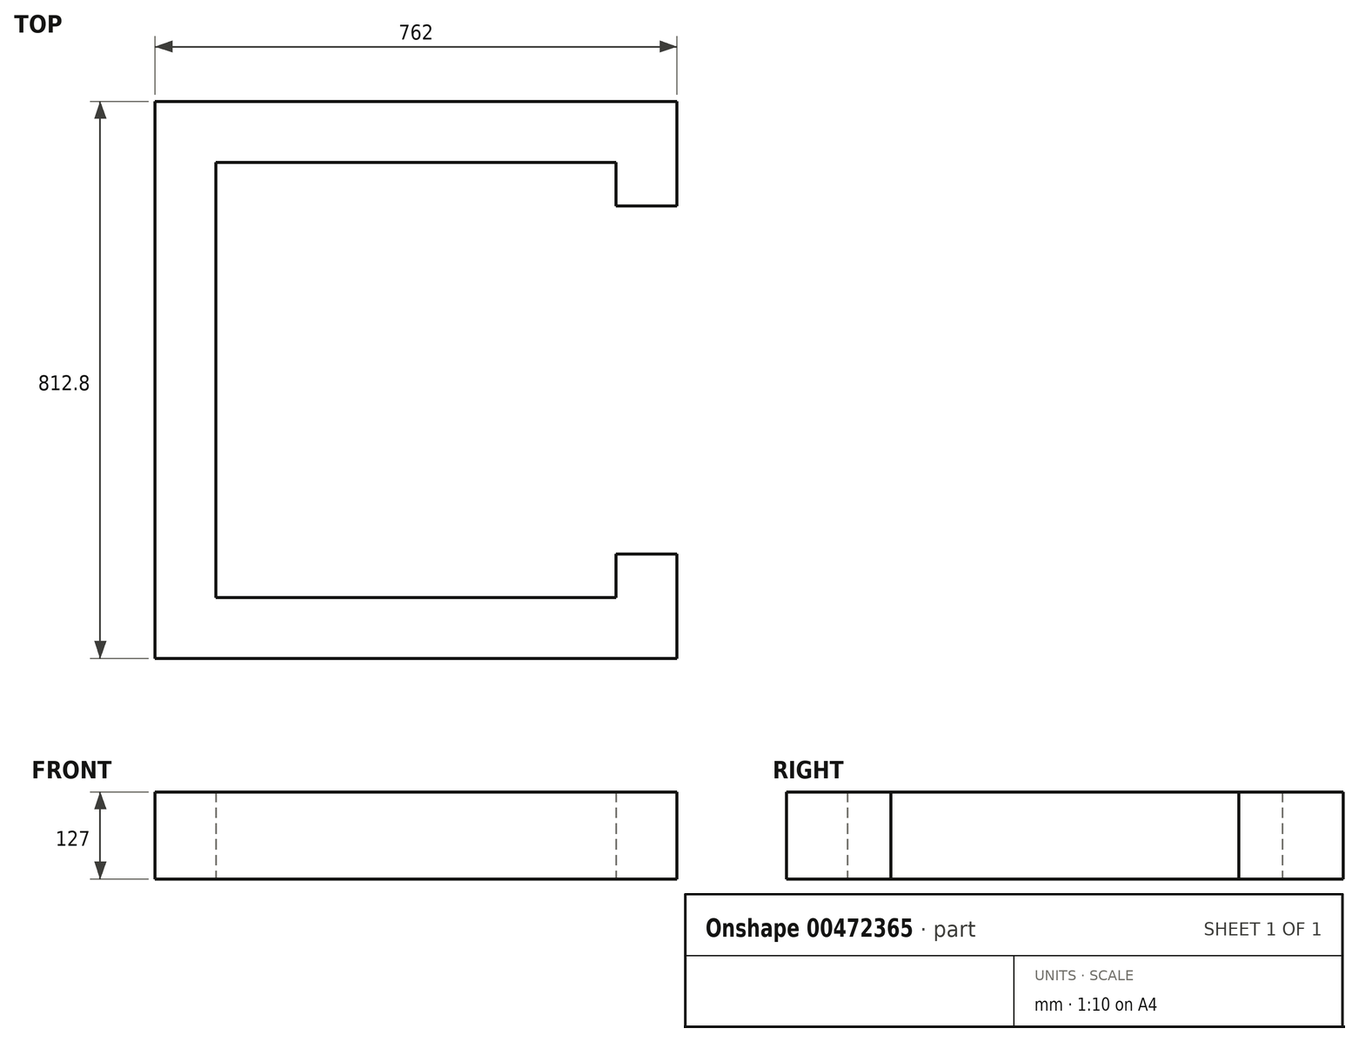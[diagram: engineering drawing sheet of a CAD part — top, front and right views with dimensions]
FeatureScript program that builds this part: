
annotation { "Feature Type Name" : "Feature", "Feature Type Description" : "" }
export const myFeature = defineFeature(function(context is Context, id is Id, definition is map)
    precondition{}
    {
        {
            var Q0;
            Q0=qCreatedBy(makeId("Top.planeOp"),FACE);
            var sketch = newSketch(context, id + "F0", { "sketchPlane" : qUnion([Q0])});
            skLineSegment(sketch, "E0.bottom", {"start": v(-444.08, 466.22) * mm, "end": v(317.92, 466.22) * mm});
            skLineSegment(sketch, "E0.top", {"start": v(-444.08, -346.58) * mm, "end": v(317.92, -346.58) * mm});
            skLineSegment(sketch, "E0.left", {"start": v(-444.08, 466.22) * mm, "end": v(-444.08, -346.58) * mm});
            skLineSegment(sketch, "E0.right", {"start": v(317.92, 466.22) * mm, "end": v(317.92, -346.58) * mm});
            skLineSegment(sketch, "E1.bottom", {"start": v(-355.18, 377.32) * mm, "end": v(229.02, 377.32) * mm});
            skLineSegment(sketch, "E1.top", {"start": v(-355.18, -257.68) * mm, "end": v(229.02, -257.68) * mm});
            skLineSegment(sketch, "E1.left", {"start": v(-355.18, 377.32) * mm, "end": v(-355.18, -257.68) * mm});
            skLineSegment(sketch, "E1.right", {"start": v(229.02, 377.32) * mm, "end": v(229.02, -257.68) * mm});
            skLineSegment(sketch, "E2", {"start": v(446.15, 313.82) * mm, "end": v(87.07, 313.82) * mm});
            skLineSegment(sketch, "E3", {"start": v(87.07, 313.82) * mm, "end": v(87.07, -194.18) * mm});
            skLineSegment(sketch, "E4", {"start": v(87.07, -194.18) * mm, "end": v(446.15, -194.18) * mm});
            skLineSegment(sketch, "E5", {"start": v(446.15, -194.18) * mm, "end": v(446.15, 313.82) * mm});
            skSolve(sketch);
        }
        {
            var Q0;
            Q0=makeQuery(id+"F0.imprint","IMPRINT",FACE,{"disambiguationData":[TD([[makeQuery(id+"F0.imprint","IMPRINT",EDGE,{"derivedFrom":sQuery(id+"F0.wireOp",EDGE,"E0.bottom")}),-1.0]])]});
            extrude(context, id + "F1", {"entities" : qUnion([Q0]), "depth" : 127 * mm});
        }
    });
